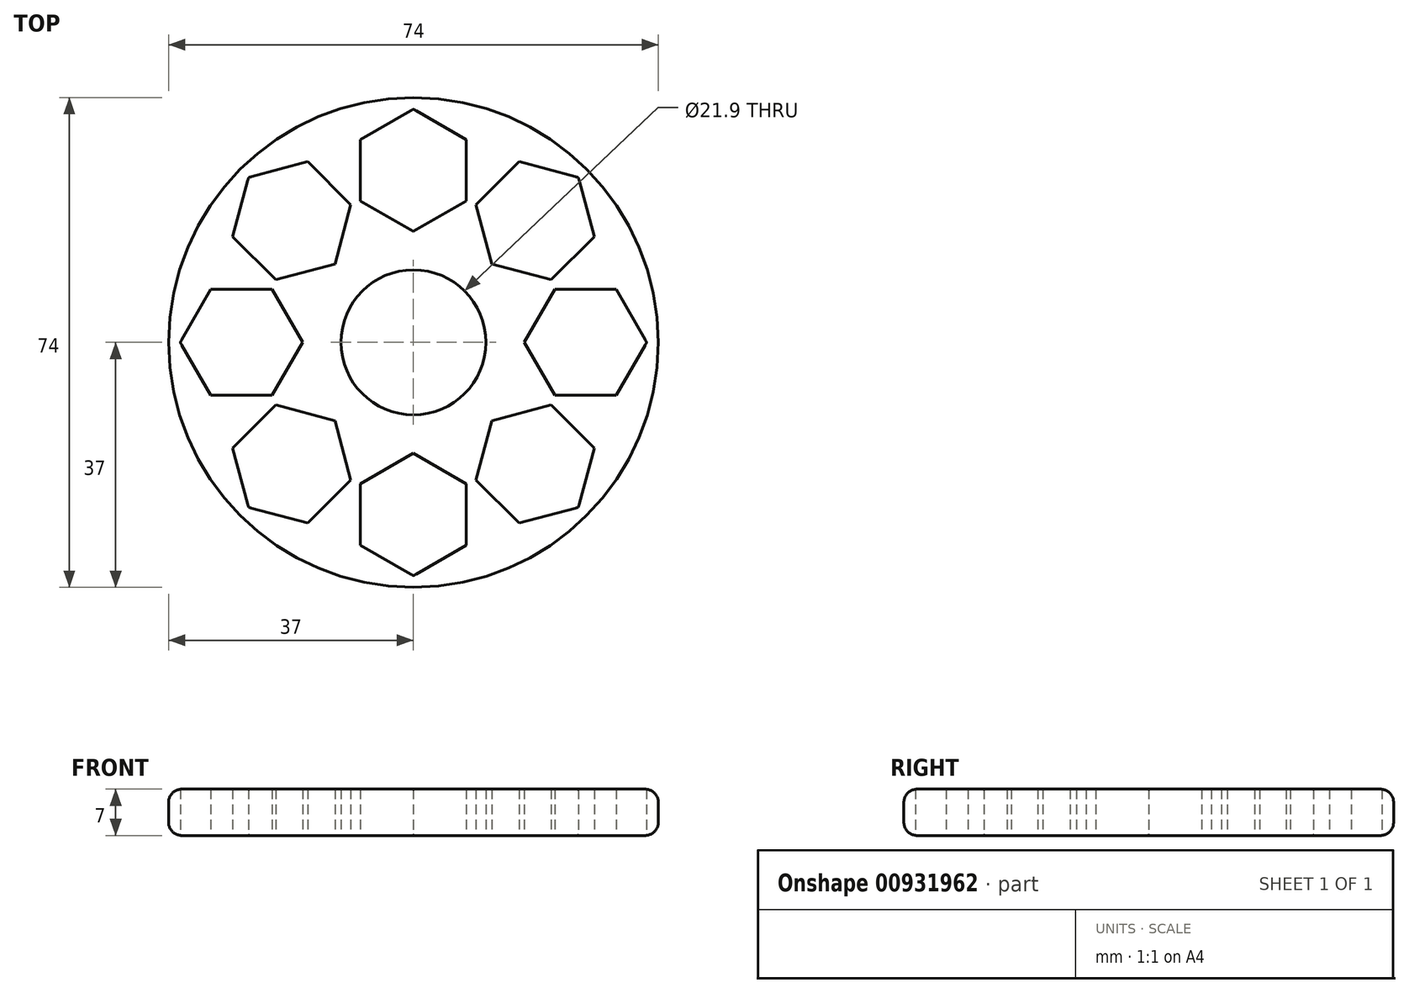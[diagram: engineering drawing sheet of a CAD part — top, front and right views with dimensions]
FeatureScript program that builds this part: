
annotation { "Feature Type Name" : "Feature", "Feature Type Description" : "" }
export const myFeature = defineFeature(function(context is Context, id is Id, definition is map)
    precondition{}
    {
        {
            var Q0;
            Q0=qCreatedBy(makeId("Top.planeOp"),FACE);
            var sketch = newSketch(context, id + "F0", { "sketchPlane" : qUnion([Q0])});
            skCircle(sketch, "E0", {"center": v(0, 0) * mm, "radius": 10.95 * mm});
            skCircle(sketch, "E1.cCircle", {"center": v(0, 26) * mm, "radius": 8 * mm, "construction": true});
            skLineSegment(sketch, "E1.0", {"start": v(8, 30.62) * mm, "end": v(8, 21.38) * mm});
            skLineSegment(sketch, "E1.1", {"start": v(8, 21.38) * mm, "end": v(0, 16.76) * mm});
            skLineSegment(sketch, "E1.2", {"start": v(0, 16.76) * mm, "end": v(-8, 21.38) * mm});
            skLineSegment(sketch, "E1.3", {"start": v(-8, 21.38) * mm, "end": v(-8, 30.62) * mm});
            skLineSegment(sketch, "E1.4", {"start": v(-8, 30.62) * mm, "end": v(0, 35.24) * mm});
            skLineSegment(sketch, "E1.5", {"start": v(0, 35.24) * mm, "end": v(8, 30.62) * mm});
            skPoint(sketch, "E1.0.midPoint", {"position": v(8, 26) * mm});
            skLineSegment(sketch, "E2.1.0", {"start": v(-24.92, 24.92) * mm, "end": v(-16, 27.3) * mm});
            skLineSegment(sketch, "E2.1.1", {"start": v(-9.46, 20.78) * mm, "end": v(-11.85, 11.85) * mm});
            skLineSegment(sketch, "E2.1.2", {"start": v(-27.3, 16) * mm, "end": v(-24.92, 24.92) * mm});
            skLineSegment(sketch, "E2.1.3", {"start": v(-11.85, 11.85) * mm, "end": v(-20.78, 9.46) * mm});
            skPoint(sketch, "E2.1.4", {"position": v(-12.73, 24.04) * mm});
            skCircle(sketch, "E2.1.5", {"center": v(-18.38, 18.38) * mm, "radius": 8 * mm, "construction": true});
            skLineSegment(sketch, "E2.1.6", {"start": v(-20.78, 9.46) * mm, "end": v(-27.3, 16) * mm});
            skLineSegment(sketch, "E2.1.7", {"start": v(-16, 27.3) * mm, "end": v(-9.46, 20.78) * mm});
            skLineSegment(sketch, "E2.2.0", {"start": v(-35.24, 0) * mm, "end": v(-30.62, 8) * mm});
            skLineSegment(sketch, "E2.2.1", {"start": v(-21.38, 8) * mm, "end": v(-16.76, 0) * mm});
            skLineSegment(sketch, "E2.2.2", {"start": v(-30.62, -8) * mm, "end": v(-35.24, 0) * mm});
            skLineSegment(sketch, "E2.2.3", {"start": v(-16.76, 0) * mm, "end": v(-21.38, -8) * mm});
            skPoint(sketch, "E2.2.4", {"position": v(-26, 8) * mm});
            skCircle(sketch, "E2.2.5", {"center": v(-26, 0) * mm, "radius": 8 * mm, "construction": true});
            skLineSegment(sketch, "E2.2.6", {"start": v(-21.38, -8) * mm, "end": v(-30.62, -8) * mm});
            skLineSegment(sketch, "E2.2.7", {"start": v(-30.62, 8) * mm, "end": v(-21.38, 8) * mm});
            skLineSegment(sketch, "E2.3.0", {"start": v(-24.92, -24.92) * mm, "end": v(-27.3, -16) * mm});
            skLineSegment(sketch, "E2.3.1", {"start": v(-20.78, -9.46) * mm, "end": v(-11.85, -11.85) * mm});
            skLineSegment(sketch, "E2.3.2", {"start": v(-16, -27.3) * mm, "end": v(-24.92, -24.92) * mm});
            skLineSegment(sketch, "E2.3.3", {"start": v(-11.85, -11.85) * mm, "end": v(-9.46, -20.78) * mm});
            skPoint(sketch, "E2.3.4", {"position": v(-24.04, -12.73) * mm});
            skCircle(sketch, "E2.3.5", {"center": v(-18.38, -18.38) * mm, "radius": 8 * mm, "construction": true});
            skLineSegment(sketch, "E2.3.6", {"start": v(-9.46, -20.78) * mm, "end": v(-16, -27.3) * mm});
            skLineSegment(sketch, "E2.3.7", {"start": v(-27.3, -16) * mm, "end": v(-20.78, -9.46) * mm});
            skLineSegment(sketch, "E2.4.0", {"start": v(0, -35.24) * mm, "end": v(-8, -30.62) * mm});
            skLineSegment(sketch, "E2.4.1", {"start": v(-8, -21.38) * mm, "end": v(0, -16.76) * mm});
            skLineSegment(sketch, "E2.4.2", {"start": v(8, -30.62) * mm, "end": v(0, -35.24) * mm});
            skLineSegment(sketch, "E2.4.3", {"start": v(0, -16.76) * mm, "end": v(8, -21.38) * mm});
            skPoint(sketch, "E2.4.4", {"position": v(-8, -26) * mm});
            skCircle(sketch, "E2.4.5", {"center": v(0, -26) * mm, "radius": 8 * mm, "construction": true});
            skLineSegment(sketch, "E2.4.6", {"start": v(8, -21.38) * mm, "end": v(8, -30.62) * mm});
            skLineSegment(sketch, "E2.4.7", {"start": v(-8, -30.62) * mm, "end": v(-8, -21.38) * mm});
            skLineSegment(sketch, "E2.5.0", {"start": v(24.92, -24.92) * mm, "end": v(16, -27.3) * mm});
            skLineSegment(sketch, "E2.5.1", {"start": v(9.46, -20.78) * mm, "end": v(11.85, -11.85) * mm});
            skLineSegment(sketch, "E2.5.2", {"start": v(27.3, -16) * mm, "end": v(24.92, -24.92) * mm});
            skLineSegment(sketch, "E2.5.3", {"start": v(11.85, -11.85) * mm, "end": v(20.78, -9.46) * mm});
            skPoint(sketch, "E2.5.4", {"position": v(12.73, -24.04) * mm});
            skCircle(sketch, "E2.5.5", {"center": v(18.38, -18.38) * mm, "radius": 8 * mm, "construction": true});
            skLineSegment(sketch, "E2.5.6", {"start": v(20.78, -9.46) * mm, "end": v(27.3, -16) * mm});
            skLineSegment(sketch, "E2.5.7", {"start": v(16, -27.3) * mm, "end": v(9.46, -20.78) * mm});
            skLineSegment(sketch, "E2.6.0", {"start": v(35.24, 0) * mm, "end": v(30.62, -8) * mm});
            skLineSegment(sketch, "E2.6.1", {"start": v(21.38, -8) * mm, "end": v(16.76, 0) * mm});
            skLineSegment(sketch, "E2.6.2", {"start": v(30.62, 8) * mm, "end": v(35.24, 0) * mm});
            skLineSegment(sketch, "E2.6.3", {"start": v(16.76, 0) * mm, "end": v(21.38, 8) * mm});
            skPoint(sketch, "E2.6.4", {"position": v(26, -8) * mm});
            skCircle(sketch, "E2.6.5", {"center": v(26, 0) * mm, "radius": 8 * mm, "construction": true});
            skLineSegment(sketch, "E2.6.6", {"start": v(21.38, 8) * mm, "end": v(30.62, 8) * mm});
            skLineSegment(sketch, "E2.6.7", {"start": v(30.62, -8) * mm, "end": v(21.38, -8) * mm});
            skLineSegment(sketch, "E2.7.0", {"start": v(24.92, 24.92) * mm, "end": v(27.3, 16) * mm});
            skLineSegment(sketch, "E2.7.1", {"start": v(20.78, 9.46) * mm, "end": v(11.85, 11.85) * mm});
            skLineSegment(sketch, "E2.7.2", {"start": v(16, 27.3) * mm, "end": v(24.92, 24.92) * mm});
            skLineSegment(sketch, "E2.7.3", {"start": v(11.85, 11.85) * mm, "end": v(9.46, 20.78) * mm});
            skPoint(sketch, "E2.7.4", {"position": v(24.04, 12.73) * mm});
            skCircle(sketch, "E2.7.5", {"center": v(18.38, 18.38) * mm, "radius": 8 * mm, "construction": true});
            skLineSegment(sketch, "E2.7.6", {"start": v(9.46, 20.78) * mm, "end": v(16, 27.3) * mm});
            skLineSegment(sketch, "E2.7.7", {"start": v(27.3, 16) * mm, "end": v(20.78, 9.46) * mm});
            skCircle(sketch, "E3", {"center": v(0, 0) * mm, "radius": 37 * mm});
            skSolve(sketch);
        }
        {
            var Q0;
            Q0=makeQuery(id+"F0.imprint","IMPRINT",FACE,{"disambiguationData":[TD([[makeQuery(id+"F0.imprint","IMPRINT",EDGE,{"derivedFrom":sQuery(id+"F0.wireOp",EDGE,"E0")}),-1.0]])]});
            extrude(context, id + "F1", {"entities" : qUnion([Q0]), "depth" : 7 * mm, "offsetDistance" : 25 * mm});
        }
        {
            var Q0;
            Q0=makeQuery(id+"F1.opExtrude","CAP_EDGE",EDGE,{"disambiguationData":[OSD([sQuery(id+"F0.wireOp",EDGE,"E3")])],"isStart":false});
            var Q1;
            Q1=makeQuery(id+"F1.opExtrude","CAP_EDGE",EDGE,{"disambiguationData":[OSD([sQuery(id+"F0.wireOp",EDGE,"E3")])],"isStart":true});
            fillet(context, id + "F2", {"entities" : qUnion([Q0, Q1]), "radius" : 2 * mm, "tangentPropagation" : true, "allowEdgeOverflow" : false});
        }
    });
